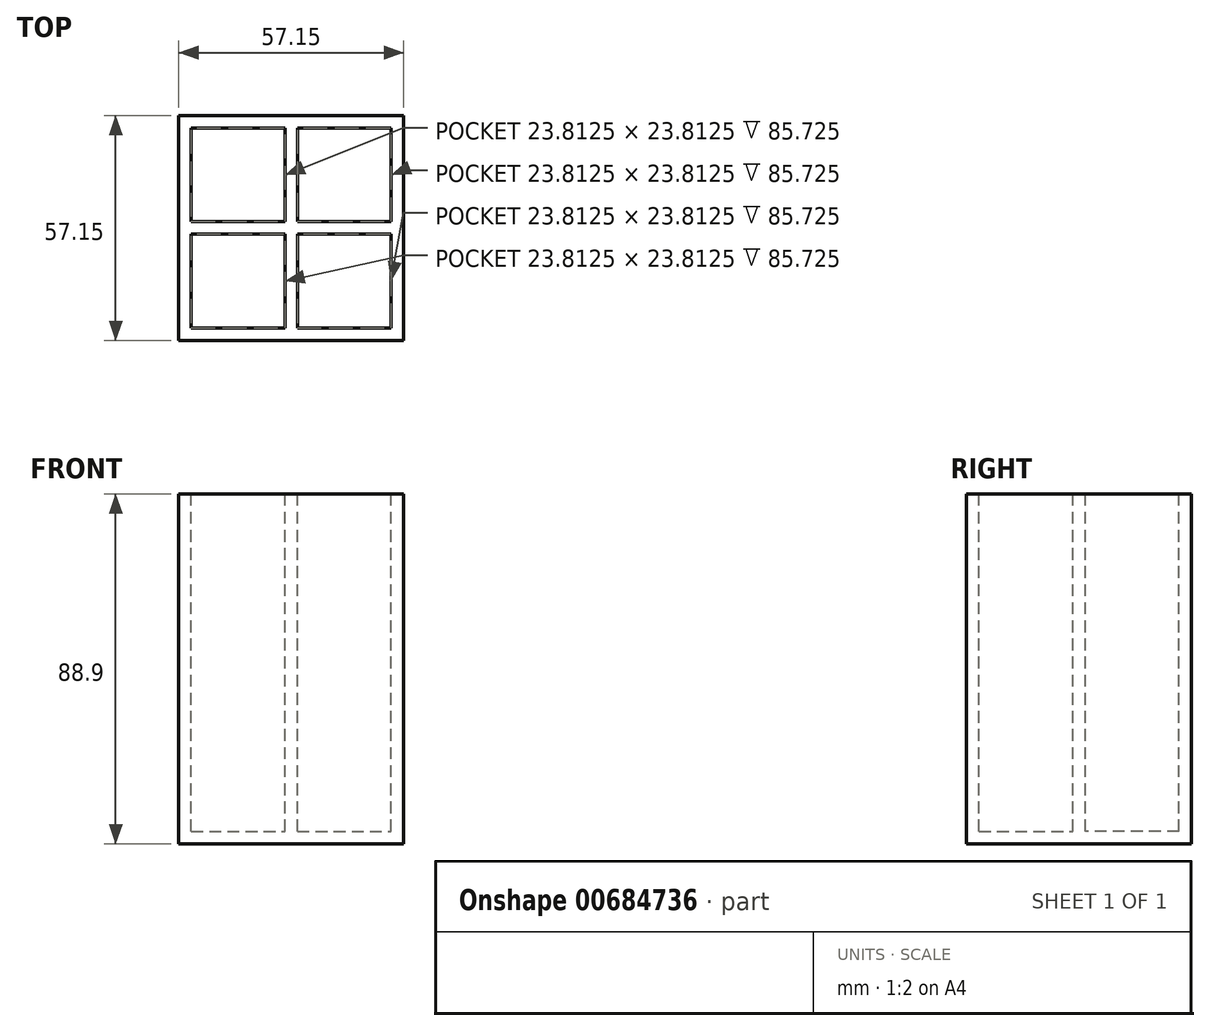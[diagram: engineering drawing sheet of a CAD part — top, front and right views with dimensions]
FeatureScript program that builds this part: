
annotation { "Feature Type Name" : "Feature", "Feature Type Description" : "" }
export const myFeature = defineFeature(function(context is Context, id is Id, definition is map)
    precondition{}
    {
        {
            var Q0;
            Q0=qCreatedBy(makeId("Top.planeOp"),FACE);
            var sketch = newSketch(context, id + "F0", { "sketchPlane" : qUnion([Q0])});
            skLineSegment(sketch, "E0.bottom", {"start": v(-28.57, 28.57) * mm, "end": v(28.58, 28.57) * mm});
            skLineSegment(sketch, "E0.top", {"start": v(-28.57, -28.58) * mm, "end": v(28.58, -28.58) * mm});
            skLineSegment(sketch, "E0.left", {"start": v(-28.57, 28.57) * mm, "end": v(-28.57, -28.58) * mm});
            skLineSegment(sketch, "E0.right", {"start": v(28.58, 28.57) * mm, "end": v(28.58, -28.58) * mm});
            skSolve(sketch);
        }
        {
            var Q0;
            Q0=makeQuery(id+"F0.imprint","IMPRINT",FACE,{"disambiguationData":[TD([[makeQuery(id+"F0.imprint","IMPRINT",EDGE,{"derivedFrom":sQuery(id+"F0.wireOp",EDGE,"E0.bottom")}),-1.0]])]});
            extrude(context, id + "F1", {"entities" : qUnion([Q0]), "depth" : 88.9 * mm, "offsetDistance" : 25.4 * mm});
        }
        {
            var Q0;
            Q0=makeQuery(id+"F1.opExtrude","CAP_FACE",FACE,{"disambiguationData":[OSD([sQuery(id+"F0.wireOp",EDGE,"E0.bottom"),sQuery(id+"F0.wireOp",EDGE,"E0.top"),sQuery(id+"F0.wireOp",EDGE,"E0.left"),sQuery(id+"F0.wireOp",EDGE,"E0.right")])],"isStart":false});
            var sketch = newSketch(context, id + "F2", { "sketchPlane" : qUnion([Q0])});
            skLineSegment(sketch, "E1.bottom", {"start": v(-25.4, 25.4) * mm, "end": v(-1.59, 25.4) * mm});
            skLineSegment(sketch, "E1.top", {"start": v(-25.4, 1.59) * mm, "end": v(-1.59, 1.59) * mm});
            skLineSegment(sketch, "E1.left", {"start": v(-25.4, 25.4) * mm, "end": v(-25.4, 1.59) * mm});
            skLineSegment(sketch, "E1.right", {"start": v(-1.59, 25.4) * mm, "end": v(-1.59, 1.59) * mm});
            skLineSegment(sketch, "E2.bottom", {"start": v(1.59, 25.4) * mm, "end": v(25.4, 25.4) * mm});
            skLineSegment(sketch, "E2.top", {"start": v(1.59, 1.59) * mm, "end": v(25.4, 1.59) * mm});
            skLineSegment(sketch, "E2.left", {"start": v(1.59, 25.4) * mm, "end": v(1.59, 1.59) * mm});
            skLineSegment(sketch, "E2.right", {"start": v(25.4, 25.4) * mm, "end": v(25.4, 1.59) * mm});
            skLineSegment(sketch, "E3.bottom", {"start": v(25.4, -25.4) * mm, "end": v(1.59, -25.4) * mm});
            skLineSegment(sketch, "E3.top", {"start": v(25.4, -1.59) * mm, "end": v(1.59, -1.59) * mm});
            skLineSegment(sketch, "E3.left", {"start": v(25.4, -25.4) * mm, "end": v(25.4, -1.59) * mm});
            skLineSegment(sketch, "E3.right", {"start": v(1.59, -25.4) * mm, "end": v(1.59, -1.59) * mm});
            skLineSegment(sketch, "E4.bottom", {"start": v(-25.4, -25.4) * mm, "end": v(-1.59, -25.4) * mm});
            skLineSegment(sketch, "E4.top", {"start": v(-25.4, -1.59) * mm, "end": v(-1.59, -1.59) * mm});
            skLineSegment(sketch, "E4.left", {"start": v(-25.4, -25.4) * mm, "end": v(-25.4, -1.59) * mm});
            skLineSegment(sketch, "E4.right", {"start": v(-1.59, -25.4) * mm, "end": v(-1.59, -1.59) * mm});
            skLineSegment(sketch, "E5.bottom", {"start": v(1.59, 1.59) * mm, "end": v(-1.59, 1.59) * mm, "construction": true});
            skLineSegment(sketch, "E5.top", {"start": v(1.59, -1.59) * mm, "end": v(-1.59, -1.59) * mm, "construction": true});
            skLineSegment(sketch, "E5.left", {"start": v(1.59, 1.59) * mm, "end": v(1.59, -1.59) * mm, "construction": true});
            skLineSegment(sketch, "E5.right", {"start": v(-1.59, 1.59) * mm, "end": v(-1.59, -1.59) * mm, "construction": true});
            skPoint(sketch, "E5.middle", {"position": v(0, 0) * mm});
            skSolve(sketch);
        }
        {
            var Q0;
            Q0=makeQuery(id+"F2.imprint","IMPRINT",FACE,{"disambiguationData":[TD([[makeQuery(id+"F2.imprint","IMPRINT",EDGE,{"derivedFrom":sQuery(id+"F2.wireOp",EDGE,"E1.bottom")}),-1.0]])]});
            var Q1;
            Q1=makeQuery(id+"F2.imprint","IMPRINT",FACE,{"disambiguationData":[TD([[makeQuery(id+"F2.imprint","IMPRINT",EDGE,{"derivedFrom":sQuery(id+"F2.wireOp",EDGE,"E2.bottom")}),-1.0]])]});
            var Q2;
            Q2=makeQuery(id+"F2.imprint","IMPRINT",FACE,{"disambiguationData":[TD([[makeQuery(id+"F2.imprint","IMPRINT",EDGE,{"derivedFrom":sQuery(id+"F2.wireOp",EDGE,"E3.bottom")}),-1.0]])]});
            var Q3;
            Q3=makeQuery(id+"F2.imprint","IMPRINT",FACE,{"disambiguationData":[TD([[makeQuery(id+"F2.imprint","IMPRINT",EDGE,{"derivedFrom":sQuery(id+"F2.wireOp",EDGE,"E4.bottom")}),1.0]])]});
            extrude(context, id + "F3", {"entities" : qUnion([Q0, Q1, Q2, Q3]), "operationType" : NewBodyOperationType.REMOVE, "oppositeDirection" : true, "depth" : 85.72 * mm, "offsetDistance" : 25.4 * mm});
        }
    });
